FCSTD DOCUMENT  (FreeCAD 1.0R39319 (Git))
Label: Assy_Stack_Module_Flight_Cam
License: All rights reserved
LicenseURL: https://en.wikipedia.org/wiki/All_rights_reserved
objects: TechDraw::DrawViewBalloon×8, TechDraw::DrawViewDimension×6, TechDraw::DrawProjGroupItem×5, App::DocumentObjectGroup×3, App::Link×3, PartDesign::CoordinateSystem×2, TechDraw::DrawSVGTemplate×2, TechDraw::DrawPage×2, App::FeaturePython×1, Spreadsheet::Sheet×1, TechDraw::DrawViewSpreadsheet×1, TechDraw::DrawViewAnnotation×1, App::Part×1, TechDraw::DrawViewSection×1, TechDraw::DrawProjGroup×1
note: 6 computed .brp shape members not serialized (recipe doc carries the construction recipe); baked Part::Feature solids carry a one-line shape summary decoded from their .brp
EXTERNAL_REF file=Assy_Stack_Module.FCStd obj=LCS_Origin
EXTERNAL_REF file=Assy_Stack_Module.FCStd obj=Assembly
EXTERNAL_REF file=Assy_Flight_Cam.FCStd obj=LCS_Origin
EXTERNAL_REF file=Assy_Flight_Cam.FCStd obj=Assembly
EXTERNAL_REF file=../../Part/Print/Variants/IRFilter_Mount_1inchround.FCStd obj=LCS_1
EXTERNAL_REF file=../../Part/Print/Variants/IRFilter_Mount_1inchround.FCStd obj=Part

FEATURE [App::DocumentObjectGroup] Parts
FEATURE [PartDesign::CoordinateSystem] LCS_Origin
  AttacherType = Attacher::AttachEngine3D
  AttachmentSupport = -> [X_Axis]
  MapMode = 2
FEATURE [App::DocumentObjectGroup] Constraints
FEATURE [App::FeaturePython] Variables  # WARN: FeaturePython — macro-defined, semantics opaque (R4)
  Type = App::PropertyContainer
FEATURE [App::DocumentObjectGroup] Configurations
FEATURE [App::Link] Assy_Stack_Module
  AttachedBy = #LCS_Origin
  AttachedTo = Parent Assembly#LCS_Origin
  LinkedObject = -> <external Assy_Stack_Module.FCStd>#Assembly
  SolverId = Asm4EE
  expr: Placement = LCS_Origin.Placement * AttachmentOffset * Assy_Stack_Module#LCS_Origin.Placement ^ -1
FEATURE [App::Link] Assy_Flight_Cam
  AttachedBy = #LCS_Origin
  AttachedTo = Assy_Stack_Module#LCS_Origin
  AttachmentOffset = pos=(0,50,-41.75) rot=(0.57735,-0.57735,0.57735;2.0944rad)
  LinkPlacement = pos=(0,50,-41.75) rot=(0.57735,-0.57735,0.57735;2.0944rad)
  LinkedObject = -> <external Assy_Flight_Cam.FCStd>#Assembly
  Placement = pos=(0,50,-41.75) rot=(0.57735,-0.57735,0.57735;2.0944rad)
  SolverId = Asm4EE
  expr: Placement = Assy_Stack_Module.Placement * Assy_Stack_Module#LCS_Origin.Placement * AttachmentOffset * Assy_Flight_Cam#LCS_Origin.Placement ^ -1
FEATURE [PartDesign::CoordinateSystem] LCS_1
  AttacherType = Attacher::AttachEngine3D
FEATURE [Spreadsheet::Sheet] Spreadsheet  label="BOM"
  cells = A1=4; B1=2; C1='ISO 7380-2 M5x10 mm screw; D1='10–15 mm; ISO 4762 optional; A2=3; B2=4; C2='Spacer; D2='-; E2='PETG or PLA; A3=2; B3=3; C3='Stack_Module; D3='-; E3='PETG or PLA; A4=1; B4=1; C4='Eyeball Assembly; D4='-; A5='Position; B5='Quantity; C5='Part; D5='Dimensions; E5='Material
FEATURE [TechDraw::DrawSVGTemplate] Template
  EditableTexts = approval_person=GitHubPR; creator=Stefan; date_of_issue=20.03.2026; document_type=Assembly Drawing; general_tolerances=na; identification_number=na; language_code=EN; part_material=na; revision_index=AAA; scale=1 : 1; sheet_number=1 / 1; title=Assy_Stack_Module_Flight_Cam
  Height = 420
  Orientation = 1
  Template = <userpath>/Documents/PiTrac/3D Printed Parts/Enclosure Version 3/Assets/PiTrac_A2_Landscape_ISO5457_minimal.svg
  Width = 594
FEATURE [TechDraw::DrawViewSpreadsheet] Sheet
  CellEnd = E5
  CellStart = A1
  Font = osifont
  LineWidth = 0.35
  LockPosition = false
  Rotation = 0
  ScaleType = 2
  Source = -> Spreadsheet
  Symbol = <blob: 5666 chars omitted>
  TextSize = 12
  X = 491.96
  Y = 97.1596
FEATURE [TechDraw::DrawViewAnnotation] Annotation
  Font = osifont
  LineSpace = 100
  LockPosition = false
  MaxWidth = -1
  Rotation = 0
  ScaleType = 0
  Text = Not all parts are shown
  TextSize = 5
  TextStyle = 0
  X = 217.611
  Y = 30.4897
FEATURE [App::Link] IRFilter_Mount_1inchround
  AttachedBy = #LCS_1
  AttachedTo = Assy_Flight_Cam#LCS_Origin
  AttachmentOffset = pos=(0,34,0) rot=(0.57735,-0.57735,0.57735;2.0944rad)
  LinkPlacement = pos=(-34,50,-41.75) rot=(0.57735,-0.57735,0.57735;4.18879rad)
  LinkedObject = -> <external ../../Part/Print/Variants/IRFilter_Mount_1inchround.FCStd>#Part
  Placement = pos=(-34,50,-41.75) rot=(0.57735,-0.57735,0.57735;4.18879rad)
  SolverId = Asm4EE
  expr: Placement = Assy_Flight_Cam.Placement * Assy_Flight_Cam#LCS_Origin.Placement * AttachmentOffset * IRFilter_Mount_1inchround#LCS_1.Placement ^ -1
FEATURE [App::Part] Assembly  label="Assy_Stack_Module_Flight_Cam"
  AssemblyType = Part::Link
  Group = -> [LCS_Origin,Constraints,Variables,Configurations,Assy_Stack_Module,Assy_Flight_Cam,LCS_1,IRFilter_Mount_1inchround]
  Origin = -> Origin
  Type = Assembly
FEATURE [TechDraw::DrawProjGroupItem] View
  CoarseView = false
  Direction = (-0.57735,0.57735,-0.577351)
  Focus = 100
  HardHidden = false
  IsoCount = 0
  IsoHidden = false
  IsoVisible = false
  LockPosition = false
  Perspective = false
  Rotation = 0
  RotationVector = (1,0,0)
  Scale = 0.5
  ScaleType = 2
  ScrubCount = 1
  SeamHidden = false
  SeamVisible = false
  SmoothHidden = false
  SmoothVisible = true
  Source = -> [Assembly]
  Type = 0
  X = 343.081
  XDirection = (0.707107,0.707107,0)
  Y = 85.3438
FEATURE [TechDraw::DrawProjGroupItem] View001  label="Front"
  CoarseView = false
  Direction = (-1,0,0)
  Focus = 100
  HardHidden = false
  IsoCount = 0
  IsoHidden = false
  IsoVisible = false
  LockPosition = true
  Perspective = false
  Rotation = 0
  RotationVector = (1,0,0)
  ScaleType = 2
  ScrubCount = 1
  SeamHidden = false
  SeamVisible = false
  SmoothHidden = false
  SmoothVisible = true
  Source = -> [Assembly]
  Type = 0
  X = 0
  XDirection = (0,1,0)
  Y = 0
FEATURE [TechDraw::DrawProjGroupItem] ProjItem001  label="Left"
  CoarseView = false
  Direction = (-1e-16,-1,0)
  Focus = 100
  HardHidden = false
  IsoCount = 0
  IsoHidden = false
  IsoVisible = false
  LockPosition = false
  Perspective = false
  Rotation = 0
  RotationVector = (1,0,0)
  ScaleType = 0
  ScrubCount = 1
  SeamHidden = false
  SeamVisible = false
  SmoothHidden = false
  SmoothVisible = true
  Source = -> [Assembly]
  Type = 1
  X = 159
  XDirection = (-1,1e-16,0)
  Y = 0
FEATURE [TechDraw::DrawViewSection] SectionView  label="Section A - A"
  BaseView = -> View001
  CoarseView = false
  CutSurfaceDisplay = 2
  Direction = (0,1,0)
  FileGeomPattern = <path>\data\Mod/TechDraw/PAT/FCPAT.pat
  FileHatchPattern = <path>\data\Mod/TechDraw/Patterns/simple.svg
  Focus = 100
  FuseBeforeCut = false
  HardHidden = false
  HatchOffset = (0,0,0)
  HatchRotation = 0
  HatchScale = 1
  IsoCount = 0
  IsoHidden = false
  IsoVisible = false
  LockPosition = false
  NameGeomPattern = Diamond
  Perspective = false
  Rotation = 90
  ScaleType = 0
  ScrubCount = 1
  SeamHidden = false
  SeamVisible = false
  SectionDirection = 4
  SectionLineStretch = 1
  SectionNormal = (0,1,0)
  SectionOrigin = (19.99,50,-39.75)
  SectionSymbol = A
  SmoothHidden = false
  SmoothVisible = true
  Source = -> [Assembly]
  TrimAfterCut = false
  UsePreviousCut = false
  X = 376.166
  XDirection = (0,0,-1)
  Y = 208.818
FEATURE [TechDraw::DrawProjGroupItem] ProjItem  label="Top"
  CoarseView = false
  Direction = (0,0,-1)
  Focus = 100
  HardHidden = false
  IsoCount = 0
  IsoHidden = false
  IsoVisible = false
  LockPosition = false
  Perspective = false
  Rotation = 0
  RotationVector = (1,0,0)
  ScaleType = 0
  ScrubCount = 1
  SeamHidden = false
  SeamVisible = false
  SmoothHidden = false
  SmoothVisible = true
  Source = -> [Assembly]
  Type = 4
  X = 0
  XDirection = (0,1,0)
  Y = -131.75
FEATURE [TechDraw::DrawProjGroup] ProjGroup
  Anchor = -> View001
  AutoDistribute = true
  LockPosition = false
  ProjectionType = 0
  Rotation = 0
  ScaleType = 0
  Source = -> [Assembly]
  Views = -> [View001,ProjItem,ProjItem001]
  X = 135.715
  Y = 324.613
  spacingX = 15
  spacingY = 15
FEATURE [TechDraw::DrawViewBalloon] Balloon
  BubbleShape = 0
  EndType = 0
  EndTypeScale = 1
  KinkLength = 5
  LockPosition = false
  OriginX = -8.10485
  OriginY = -28.1923
  Rotation = 0
  ScaleType = 0
  ShapeScale = 1
  SourceView = -> ProjItem
  Text = 1
  TextWrapLen = -1
  X = -90
  Y = -44.8211
FEATURE [TechDraw::DrawViewBalloon] Balloon001
  BubbleShape = 0
  EndType = 0
  EndTypeScale = 1
  KinkLength = 5
  LockPosition = false
  OriginX = -59
  OriginY = 4.65153
  Rotation = 0
  ScaleType = 0
  ShapeScale = 1
  SourceView = -> ProjItem
  Text = 2
  TextWrapLen = -1
  X = -90
  Y = 7.51869
FEATURE [TechDraw::DrawViewBalloon] Balloon002
  BubbleShape = 0
  EndType = 0
  EndTypeScale = 1
  KinkLength = 5
  LockPosition = false
  OriginX = -63.6389
  OriginY = -53.0053
  Rotation = 0
  ScaleType = 0
  ShapeScale = 1
  SourceView = -> ProjItem
  Text = 3
  TextWrapLen = -1
  X = -90
  Y = -71.4065
FEATURE [TechDraw::DrawViewBalloon] Balloon003
  BubbleShape = 0
  EndType = 0
  EndTypeScale = 1
  KinkLength = 5
  LockPosition = false
  OriginX = 63.25
  OriginY = -53.5
  Rotation = 0
  ScaleType = 0
  ShapeScale = 1
  SourceView = -> ProjItem
  Text = 3
  TextWrapLen = -1
  X = 90
  Y = -71.3104
FEATURE [TechDraw::DrawViewBalloon] Balloon005
  BubbleShape = 0
  EndType = 0
  EndTypeScale = 1
  KinkLength = 5
  LockPosition = false
  OriginX = 60.25
  OriginY = 62.5
  Rotation = 0
  ScaleType = 0
  ShapeScale = 1
  SourceView = -> ProjItem
  Text = 3
  TextWrapLen = -1
  X = 90
  Y = 35.237
FEATURE [TechDraw::DrawViewBalloon] Balloon006
  BubbleShape = 0
  EndType = 0
  EndTypeScale = 1
  KinkLength = 5
  LockPosition = false
  OriginX = -59.5034
  OriginY = 64.5614
  Rotation = 0
  ScaleType = 0
  ShapeScale = 1
  SourceView = -> ProjItem
  Text = 3
  TextWrapLen = -1
  X = -90
  Y = 62.1115
FEATURE [TechDraw::DrawViewBalloon] Balloon007
  BubbleShape = 0
  EndType = 0
  EndTypeScale = 1
  KinkLength = 5
  LockPosition = false
  OriginX = -51.8231
  OriginY = -46.9426
  Rotation = 0
  ScaleType = 0
  ShapeScale = 1
  SourceView = -> View001
  Text = 4
  TextWrapLen = -1
  X = -90
  Y = -51.1449
FEATURE [TechDraw::DrawViewBalloon] Balloon008
  BubbleShape = 0
  EndType = 0
  EndTypeScale = 1
  KinkLength = 5
  LockPosition = false
  OriginX = 52.1555
  OriginY = -45.761
  Rotation = 0
  ScaleType = 0
  ShapeScale = 1
  SourceView = -> View001
  Text = 4
  TextWrapLen = -1
  X = 90
  Y = -74.0359
FEATURE [TechDraw::DrawViewDimension] Dimension001
  AngleOverride = false
  Arbitrary = false
  ArbitraryTolerances = false
  BoxCorners = (2) [(-74,-70,-1e-07),(74,70,1e-07)]
  EqualTolerance = true
  ExtensionAngle = 0
  FormatSpec = %.2w
  FormatSpecOverTolerance = %+.2w
  FormatSpecUnderTolerance = %+.2w
  Inverted = false
  LineAngle = 0
  LockPosition = false
  MeasureType = 1
  OverTolerance = 0
  References2D = -> [ProjItem]
  Rotation = 0
  ScaleType = 0
  TheoreticalExact = false
  Type = 0
  UnderTolerance = 0
  X = -3.00169
  Y = -115.966
FEATURE [TechDraw::DrawViewDimension] Dimension002
  AngleOverride = false
  Arbitrary = false
  ArbitraryTolerances = false
  BoxCorners = (2) [(-70,-46,-1e-07),(70,46,1e-07)]
  EqualTolerance = true
  ExtensionAngle = 0
  FormatSpec = %.2w
  FormatSpecOverTolerance = %+.2w
  FormatSpecUnderTolerance = %+.2w
  Inverted = false
  LineAngle = 0
  LockPosition = false
  MeasureType = 1
  OverTolerance = 0
  References2D = -> [ProjItem001]
  Rotation = 0
  ScaleType = 0
  TheoreticalExact = false
  Type = 0
  UnderTolerance = 0
  X = 110.964
  Y = 0.25
FEATURE [TechDraw::DrawViewDimension] Dimension003
  AngleOverride = false
  Arbitrary = false
  ArbitraryTolerances = false
  BoxCorners = (2) [(-70,-46,-1e-07),(70,46,1e-07)]
  EqualTolerance = true
  ExtensionAngle = 0
  FormatSpec = %.2w
  FormatSpecOverTolerance = %+.2w
  FormatSpecUnderTolerance = %+.2w
  Inverted = false
  LineAngle = 0
  LockPosition = false
  MeasureType = 1
  OverTolerance = 0
  References2D = -> [ProjItem001]
  Rotation = 0
  ScaleType = 0
  TheoreticalExact = false
  Type = 0
  UnderTolerance = 0
  X = 149.356
  Y = 1.25
FEATURE [TechDraw::DrawViewDimension] Dimension004
  AngleOverride = false
  Arbitrary = false
  ArbitraryTolerances = false
  BoxCorners = (2) [(-74,-70,-1e-07),(74,70,1e-07)]
  EqualTolerance = true
  ExtensionAngle = 0
  FormatSpec = %.2w
  FormatSpecOverTolerance = %+.2w
  FormatSpecUnderTolerance = %+.2w
  Inverted = false
  LineAngle = 0
  LockPosition = false
  MeasureType = 1
  OverTolerance = 0
  References2D = -> [ProjItem]
  Rotation = 0
  ScaleType = 0
  TheoreticalExact = false
  Type = 0
  UnderTolerance = 0
  X = 126.237
  Y = 5
FEATURE [TechDraw::DrawSVGTemplate] Template001
  Height = 210
  Orientation = 1
  Template = C:/Program Files/FreeCAD 1.0/data/Mod/TechDraw/Templates/Default_Template_A4_Landscape.svg
  Width = 297
FEATURE [TechDraw::DrawProjGroupItem] View002
  CoarseView = false
  Direction = (-0.57735,0.57735,-0.577351)
  Focus = 100
  HardHidden = false
  IsoCount = 0
  IsoHidden = false
  IsoVisible = false
  LockPosition = false
  Perspective = false
  Rotation = 0
  RotationVector = (1,0,0)
  ScaleType = 0
  ScrubCount = 1
  SeamHidden = false
  SeamVisible = false
  SmoothHidden = false
  SmoothVisible = true
  Source = -> [Assembly]
  Type = 0
  X = 148.5
  XDirection = (0.707107,0.707107,0)
  Y = 105
FEATURE [TechDraw::DrawPage] Page001
  KeepUpdated = true
  NextBalloonIndex = 1
  ProjectionType = 0
  Template = -> Template001
  Views = -> [View002]
FEATURE [TechDraw::DrawViewDimension] Dimension
  AngleOverride = false
  Arbitrary = false
  ArbitraryTolerances = false
  BoxCorners = (2) [(-74,-70,-1e-07),(74,70,1e-07)]
  EqualTolerance = true
  ExtensionAngle = 0
  FormatSpec = %.1w
  FormatSpecOverTolerance = %+.2w
  FormatSpecUnderTolerance = %+.2w
  Inverted = false
  LineAngle = 0
  LockPosition = false
  MeasureType = 1
  OverTolerance = 0
  References2D = -> [ProjItem]
  Rotation = 0
  ScaleType = 0
  TheoreticalExact = false
  Type = 2
  UnderTolerance = 0
  X = 103.142
  Y = -44.9928
FEATURE [TechDraw::DrawViewDimension] Dimension005
  AngleOverride = false
  Arbitrary = false
  ArbitraryTolerances = false
  BoxCorners = (2) [(-70,-46.125,-1e-07),(70,46.125,1e-07)]
  EqualTolerance = true
  ExtensionAngle = 0
  FormatSpec = %.1w
  FormatSpecOverTolerance = %+.2w
  FormatSpecUnderTolerance = %+.2w
  Inverted = false
  LineAngle = 0
  LockPosition = false
  MeasureType = 1
  OverTolerance = 0
  References2D = -> [SectionView]
  Rotation = 0
  ScaleType = 0
  TheoreticalExact = false
  Type = 0
  UnderTolerance = 0
  X = -39.9928
  Y = -51.5552
FEATURE [TechDraw::DrawPage] Page
  KeepUpdated = true
  NextBalloonIndex = 11
  ProjectionType = 0
  Template = -> Template
  Views = -> [Sheet,View,ProjGroup,SectionView,Balloon,Balloon001,Balloon002,Balloon003,Balloon005,Balloon006,Balloon007,Balloon008,Dimension001,Dimension002,Dimension003,Dimension004,Annotation,Dimension,Dimension005]
note: 2 file-system paths scrubbed to <path> (originals preserved in the JSON sidecar)

RESOLVED EXTERNAL PARTS (link-assembly join: the EXTERNAL_REF files above that resolve inside this repo's crawl, each included once):
---- part ../../Part/Print/Variants/IRFilter_Mount_1inchround.FCStd = doc fcstd_7a37d6c983e9 ----
FCSTD DOCUMENT  (FreeCAD 1.0R39319 (Git))
Label: IRFilter_Mount_1inchround
License: All rights reserved
LicenseURL: https://en.wikipedia.org/wiki/All_rights_reserved
objects: Sketcher::SketchObject×3, PartDesign::Pad×1, PartDesign::Groove×1, PartDesign::Pocket×1, PartDesign::PolarPattern×1, PartDesign::Body×1, PartDesign::CoordinateSystem×1, App::Part×1
note: 19 computed .brp shape members not serialized (recipe doc carries the construction recipe); baked Part::Feature solids carry a one-line shape summary decoded from their .brp

FEATURE [Sketcher::SketchObject] Sketch
  ArcFitTolerance = 1e-06
  AttachmentSupport = -> [XY_Plane001]
  FullyConstrained = true
  MakeInternals = false
  MapMode = 5
  sketch-geometry (1):
    g0: Circle CenterX=0 CenterY=0 CenterZ=0 NormalX=0 NormalY=0 NormalZ=1 AngleXU=0 Radius=17
  constraints (2):
    c: Coincident(g0,g-1)
    c: Diameter(g0) = 34
FEATURE [PartDesign::Pad] Pad
  Direction = (0,0,1)
  Length = 10
  Length2 = 10
  Profile = -> Sketch
  ReferenceAxis = -> Sketch [N_Axis]
  Refine = true
  Suppressed = false
  Type = 0
FEATURE [Sketcher::SketchObject] Sketch001
  ArcFitTolerance = 1e-06
  AttachmentSupport = -> [YZ_Plane001]
  ExternalGeometry = -> [Pad]
  FullyConstrained = true
  MakeInternals = false
  MapMode = 5
  Placement = pos=(0,0,0) rot=(0.57735,0.57735,0.57735;2.0944rad)
  sketch-geometry (13):
    g0: LineSegment StartX=0 StartY=0 StartZ=0 EndX=0 EndY=10 EndZ=0
    g1: LineSegment StartX=0 StartY=10 StartZ=0 EndX=16 EndY=10 EndZ=0
    g2: LineSegment StartX=16 StartY=10 StartZ=0 EndX=15 EndY=8.26795 EndZ=0
    g3: LineSegment StartX=15 StartY=8.26795 StartZ=0 EndX=16 EndY=1.5 EndZ=0
    g4: LineSegment StartX=16 StartY=1.5 StartZ=0 EndX=13.7 EndY=1.5 EndZ=0
    g5: LineSegment StartX=13.7 StartY=1.5 StartZ=0 EndX=13.7 EndY=2.7 EndZ=0
    g6: LineSegment StartX=13.7 StartY=2.7 StartZ=0 EndX=13.1 EndY=2.7 EndZ=0
    g7: LineSegment StartX=13.1 StartY=2.7 StartZ=0 EndX=13.1 EndY=1.5 EndZ=0
    g8: LineSegment StartX=13.1 StartY=1.5 StartZ=0 EndX=12.6 EndY=1.5 EndZ=0
    g9: LineSegment StartX=12.6 StartY=1.5 StartZ=0 EndX=12.6 EndY=0 EndZ=0
    g10: LineSegment StartX=12.6 StartY=0 StartZ=0 EndX=0 EndY=0 EndZ=0
    g11: LineSegment [constr] StartX=13.1 StartY=1.5 StartZ=0 EndX=13.7 EndY=1.5 EndZ=0
    g12: LineSegment [constr] StartX=16 StartY=1.5 StartZ=0 EndX=16 EndY=10 EndZ=0
  constraints (36):
    c: Coincident(g-1,g0)
    c: PointOnObject(g0,g-2)
    c: Coincident(g0,g1)
    c: Horizontal(g1)
    c: Coincident(g1,g2)
    c: Coincident(g2,g3)
    c: Coincident(g3,g4)
    c: Horizontal(g4)
    c: Coincident(g4,g5)
    c: Vertical(g5)
    c: Coincident(g5,g6)
    c: Horizontal(g6)
    c: Coincident(g6,g7)
    c: Vertical(g7)
    c: Coincident(g7,g8)
    c: Horizontal(g8)
    c: Coincident(g8,g9)
    c: PointOnObject(g9,g-1)
    c: Coincident(g9,g10)
    c: Coincident(g10,g0)
    c: PointOnObject(g0,g-3)
    c: Angle(g1,g2) = 1.0472
    c: Vertical(g9)
    c: Distance(g7,g9) = 0.5
    c: Distance(g5,g7) = 0.6
    c: Distance(g6,g4) = 1.2
    c: Distance(g8,g10) = 1.5
    c: DistanceX(g-1,g2) = 15
    c: DistanceX(g-1,g1) = 16
    c: Coincident(g11,g7)
    c: Coincident(g11,g4)
    c: Coincident(g12,g3)
    c: Coincident(g12,g1)
    c: Vertical(g12)
    c: Horizontal(g11)
    c: DistanceX(g-1,g6) = 13.1
FEATURE [PartDesign::Groove] Groove
  Angle = 360
  Angle2 = 60
  Axis = (0,0,1)
  Base = (0,0,0)
  BaseFeature = -> Pad
  Profile = -> Sketch001
  ReferenceAxis = -> Sketch001 [V_Axis]
  Refine = true
  Suppressed = false
  Type = 0
FEATURE [Sketcher::SketchObject] Sketch002
  ArcFitTolerance = 1e-06
  AttachmentSupport = -> [XZ_Plane001]
  ExternalGeometry = -> [Groove]
  FullyConstrained = true
  MakeInternals = false
  MapMode = 5
  Placement = pos=(0,0,0) rot=(1,0,0;1.5708rad)
  sketch-geometry (4):
    g0: LineSegment StartX=-1.25 StartY=10 StartZ=0 EndX=1.25 EndY=10 EndZ=0
    g1: LineSegment StartX=1.25 StartY=10 StartZ=0 EndX=1.25 EndY=5 EndZ=0
    g2: ArcOfCircle CenterX=-1e-16 CenterY=5 CenterZ=0 NormalX=0 NormalY=0 NormalZ=1 AngleXU=0 Radius=1.25 StartAngle=3.14159 EndAngle=6.28319
    g3: LineSegment StartX=-1.25 StartY=5 StartZ=0 EndX=-1.25 EndY=10 EndZ=0
  constraints (10):
    c: Coincident(g0,g1)
    c: Vertical(g1)
    c: Tangent(g1,g2) = 1.5708
    c: Tangent(g2,g3) = 1.5708
    c: Coincident(g3,g0)
    c: Vertical(g3)
    c: Distance(g1,g3) = 2.5
    c: PointOnObject(g0,g-3)
    c: Symmetric(g0,g0,g-2)
    c: Distance(g2,g0) = 5
FEATURE [PartDesign::Pocket] Pocket
  BaseFeature = -> Groove
  Direction = (0,1,-2e-16)
  Length = 5
  Length2 = 5
  Midplane = true
  Profile = -> Sketch002
  ReferenceAxis = -> Sketch002 [N_Axis]
  Refine = true
  Suppressed = false
  Type = 1
FEATURE [PartDesign::PolarPattern] PolarPattern
  Angle = 90
  Axis = -> Z_Axis001
  BaseFeature = -> Pocket
  Mode = 0
  Occurrences = 2
  Offset = 120
  Originals = -> [Pocket]
  Refine = true
  Suppressed = false
  TransformMode = 0
FEATURE [PartDesign::Body] Body
  AllowCompound = false
  Group = -> [Sketch,Pad,Sketch001,Groove,Sketch002,Pocket,PolarPattern]
  Origin = -> Origin001
  Tip = -> PolarPattern
FEATURE [PartDesign::CoordinateSystem] LCS_1
  AttacherType = Attacher::AttachEngine3D
FEATURE [App::Part] Part  label="IRFilter_Mount_1inchround"
  Group = -> [Body,LCS_1]
  Origin = -> Origin
---- part Assy_Flight_Cam.FCStd = doc fcstd_9f404098250c ----
FCSTD DOCUMENT  (FreeCAD 1.0R39319 (Git))
Label: Assy_Flight_Cam
License: All rights reserved
LicenseURL: https://en.wikipedia.org/wiki/All_rights_reserved
objects: TechDraw::DrawViewBalloon×11, TechDraw::DrawProjGroupItem×7, TechDraw::DrawViewDimension×4, App::DocumentObjectGroup×3, App::Link×3, TechDraw::DrawSVGTemplate×2, TechDraw::DrawPage×2, PartDesign::CoordinateSystem×1, App::FeaturePython×1, App::Part×1, TechDraw::DrawViewSection×1, TechDraw::DrawProjGroup×1, Spreadsheet::Sheet×1, TechDraw::DrawViewSpreadsheet×1, TechDraw::DrawViewAnnotation×1
note: 9 computed .brp shape members not serialized (recipe doc carries the construction recipe); baked Part::Feature solids carry a one-line shape summary decoded from their .brp
EXTERNAL_REF file=Assy_Camera_Eyeball.FCStd obj=LCS_Origin
EXTERNAL_REF file=Assy_Camera_Eyeball.FCStd obj=Assembly
EXTERNAL_REF file=Assy_EyeScreen.FCStd obj=LCS_Origin
EXTERNAL_REF file=Assy_EyeScreen.FCStd obj=Assembly
EXTERNAL_REF file=Assy_EyeScreen_Clamp.FCStd obj=LCS_Origin
EXTERNAL_REF file=Assy_EyeScreen_Clamp.FCStd obj=Assembly

FEATURE [App::DocumentObjectGroup] Parts
FEATURE [PartDesign::CoordinateSystem] LCS_Origin
  AttacherType = Attacher::AttachEngine3D
  AttachmentSupport = -> [X_Axis]
  MapMode = 2
FEATURE [App::DocumentObjectGroup] Constraints
FEATURE [App::FeaturePython] Variables  # WARN: FeaturePython — macro-defined, semantics opaque (R4)
  Type = App::PropertyContainer
FEATURE [App::DocumentObjectGroup] Configurations
FEATURE [App::Link] Assy_Camera_Eyeball
  AttachedBy = #LCS_Origin
  AttachedTo = Parent Assembly#LCS_Origin
  LinkedObject = -> <external Assy_Camera_Eyeball.FCStd>#Assembly
  SolverId = Asm4EE
  expr: Placement = LCS_Origin.Placement * AttachmentOffset * Assy_Camera_Eyeball#LCS_Origin.Placement ^ -1
FEATURE [App::Link] Assy_EyeScreen
  AttachedBy = #LCS_Origin
  AttachedTo = Parent Assembly#LCS_Origin
  AttachmentOffset = pos=(0,0,0) rot=(0.57735,0.57735,-0.57735;4.18879rad)
  LinkPlacement = pos=(0,0,0) rot=(0.57735,0.57735,-0.57735;4.18879rad)
  LinkedObject = -> <external Assy_EyeScreen.FCStd>#Assembly
  Placement = pos=(0,0,0) rot=(0.57735,0.57735,-0.57735;4.18879rad)
  SolverId = Asm4EE
  expr: Placement = LCS_Origin.Placement * AttachmentOffset * Assy_EyeScreen#LCS_Origin.Placement ^ -1
FEATURE [App::Link] Assy_EyeScreen_Clamp
  AttachedBy = #LCS_Origin
  AttachedTo = Parent Assembly#LCS_Origin
  AttachmentOffset = pos=(0,0,0) rot=(-0.57735,-0.57735,0.57735;4.18879rad)
  LinkPlacement = pos=(0,0,0) rot=(-0.57735,-0.57735,0.57735;4.18879rad)
  LinkedObject = -> <external Assy_EyeScreen_Clamp.FCStd>#Assembly
  Placement = pos=(0,0,0) rot=(-0.57735,-0.57735,0.57735;4.18879rad)
  SolverId = Asm4EE
  expr: Placement = LCS_Origin.Placement * AttachmentOffset * Assy_EyeScreen_Clamp#LCS_Origin.Placement ^ -1
FEATURE [App::Part] Assembly  label="Assy_Flight_Cam"
  AssemblyType = Part::Link
  Group = -> [LCS_Origin,Constraints,Variables,Configurations,Assy_Camera_Eyeball,Assy_EyeScreen,Assy_EyeScreen_Clamp]
  Origin = -> Origin
  Type = Assembly
FEATURE [TechDraw::DrawSVGTemplate] Template
  EditableTexts = approval_person=GitHubPR; creator=Stefan; date_of_issue=20.03.2026; document_type=Assembly Drawing; general_tolerances=na; identification_number=na; language_code=EN; part_material=na; revision_index=AAA; scale=1 : 1; sheet_number=1 / 1; title=Assy_Flight_Cam
  Height = 420
  Orientation = 1
  Template = <userpath>/Documents/PiTrac/3D Printed Parts/Enclosure Version 3/Assets/PiTrac_A2_Landscape_ISO5457_minimal.svg
  Width = 594
FEATURE [TechDraw::DrawProjGroupItem] View
  CoarseView = false
  Direction = (-0.57735,0.57735,-0.57735)
  Focus = 100
  HardHidden = false
  IsoCount = 0
  IsoHidden = false
  IsoVisible = false
  LockPosition = false
  Perspective = false
  Rotation = 0
  RotationVector = (1,0,0)
  ScaleType = 0
  ScrubCount = 1
  SeamHidden = false
  SeamVisible = false
  SmoothHidden = false
  SmoothVisible = true
  Source = -> [Assembly]
  Type = 0
  X = 339.537
  XDirection = (0,-0.707106,-0.707106)
  Y = 100.114
FEATURE [TechDraw::DrawProjGroupItem] View001  label="Front"
  CoarseView = false
  Direction = (0,1,0)
  Focus = 100
  HardHidden = false
  IsoCount = 0
  IsoHidden = false
  IsoVisible = false
  LockPosition = true
  Perspective = false
  Rotation = 0
  RotationVector = (1,0,0)
  ScaleType = 2
  ScrubCount = 1
  SeamHidden = false
  SeamVisible = false
  SmoothHidden = false
  SmoothVisible = true
  Source = -> [Assembly]
  Type = 0
  X = 0
  XDirection = (0,0,-1)
  Y = 0
FEATURE [TechDraw::DrawProjGroupItem] ProjItem  label="Top"
  CoarseView = false
  Direction = (-1,0,0)
  Focus = 100
  HardHidden = false
  IsoCount = 0
  IsoHidden = false
  IsoVisible = false
  LockPosition = false
  Perspective = false
  Rotation = 0
  RotationVector = (1,0,0)
  ScaleType = 0
  ScrubCount = 1
  SeamHidden = false
  SeamVisible = false
  SmoothHidden = false
  SmoothVisible = true
  Source = -> [Assembly]
  Type = 4
  X = 0
  XDirection = (0,0,-1)
  Y = -87.3862
FEATURE [TechDraw::DrawProjGroupItem] ProjItem001  label="Left"
  CoarseView = false
  Direction = (0,1e-16,1)
  Focus = 100
  HardHidden = false
  IsoCount = 0
  IsoHidden = false
  IsoVisible = false
  LockPosition = false
  Perspective = false
  Rotation = 0
  RotationVector = (1,0,0)
  ScaleType = 0
  ScrubCount = 1
  SeamHidden = false
  SeamVisible = false
  SmoothHidden = false
  SmoothVisible = true
  Source = -> [Assembly]
  Type = 1
  X = 98.664
  XDirection = (0,1,-1e-16)
  Y = 0
FEATURE [TechDraw::DrawProjGroupItem] ProjItem002  label="Rear"
  CoarseView = false
  Direction = (0,-1,0)
  Focus = 100
  HardHidden = false
  IsoCount = 0
  IsoHidden = false
  IsoVisible = false
  LockPosition = false
  Perspective = false
  Rotation = 0
  RotationVector = (1,0,0)
  ScaleType = 0
  ScrubCount = 1
  SeamHidden = false
  SeamVisible = false
  SmoothHidden = false
  SmoothVisible = true
  Source = -> [Assembly]
  Type = 3
  X = 197.325
  XDirection = (0,0,1)
  Y = 0
FEATURE [TechDraw::DrawViewSection] SectionView  label="Section A - A"
  BaseView = -> View001
  CoarseView = false
  CutSurfaceDisplay = 2
  Direction = (-1,0,-1e-16)
  FileGeomPattern = <path>\data\Mod/TechDraw/PAT/FCPAT.pat
  FileHatchPattern = <path>\data\Mod/TechDraw/Patterns/simple.svg
  Focus = 100
  FuseBeforeCut = false
  HardHidden = false
  HatchOffset = (0,0,0)
  HatchRotation = 0
  HatchScale = 1
  IsoCount = 0
  IsoHidden = false
  IsoVisible = false
  LockPosition = false
  NameGeomPattern = Diamond
  Perspective = false
  Rotation = 0
  ScaleType = 0
  ScrubCount = 1
  SeamHidden = false
  SeamVisible = false
  SectionDirection = 4
  SectionLineStretch = 1
  SectionNormal = (-1,0,-1e-16)
  SectionOrigin = (0,3.24,0)
  SectionSymbol = A
  SmoothHidden = false
  SmoothVisible = true
  Source = -> [Assembly]
  TrimAfterCut = false
  UsePreviousCut = false
  X = 132.761
  XDirection = (1e-16,0,-1)
  Y = 93.6148
FEATURE [TechDraw::DrawProjGroupItem] ProjItem003  label="Bottom"
  CoarseView = false
  Direction = (1,0,0)
  Focus = 100
  HardHidden = false
  IsoCount = 0
  IsoHidden = false
  IsoVisible = false
  LockPosition = false
  Perspective = false
  Rotation = 0
  RotationVector = (1,0,0)
  ScaleType = 0
  ScrubCount = 1
  SeamHidden = false
  SeamVisible = false
  SmoothHidden = false
  SmoothVisible = true
  Source = -> [Assembly]
  Type = 5
  X = 0
  XDirection = (0,0,-1)
  Y = 87.3862
FEATURE [TechDraw::DrawProjGroup] ProjGroup
  Anchor = -> View001
  AutoDistribute = true
  LockPosition = false
  ProjectionType = 0
  Rotation = 0
  ScaleType = 0
  Source = -> [Assembly]
  Views = -> [View001,ProjItem,ProjItem001,ProjItem002,ProjItem003]
  X = 132.761
  Y = 274.987
  spacingX = 15
  spacingY = 15
FEATURE [Spreadsheet::Sheet] Spreadsheet  label="BOM"
  cells = A1=5; B1=4; C1='ISO 7380-2 M5x20 mm screw; D1='20–25 mm; ISO 4762 optional; A2=4; B2=4; C2='ISO 4032 M5 nut; A3=3; B3=1; C3='EyeScreen_Clamp; D3='8-12 mm ; E3='PETG or PLA; A4=2; B4=1; C4='EyeScreen; D4='-; E4='PETG or PLA; A5=1; B5=1; C5='Camera or LED Assembly; D5='-; A6='Position; B6='Quantity; C6='Part; D6='Dimensions; E6='Material
FEATURE [TechDraw::DrawViewSpreadsheet] Sheet
  CellEnd = E6
  CellStart = A1
  Font = osifont
  LineWidth = 0.35
  LockPosition = false
  Rotation = 0
  ScaleType = 2
  Source = -> Spreadsheet
  Symbol = <blob: 6751 chars omitted>
  TextSize = 12
  X = 491.96
  Y = 112.52
FEATURE [TechDraw::DrawViewBalloon] Balloon
  BubbleShape = 0
  EndType = 0
  EndTypeScale = 1
  KinkLength = 5
  LockPosition = false
  OriginX = -14.5739
  OriginY = -27.7259
  Rotation = 0
  ScaleType = 0
  ShapeScale = 1
  SourceView = -> ProjItem
  Text = 1
  TextWrapLen = -1
  X = -85
  Y = -42.6008
FEATURE [TechDraw::DrawViewBalloon] Balloon001
  BubbleShape = 0
  EndType = 0
  EndTypeScale = 1
  KinkLength = 5
  LockPosition = false
  OriginX = -13.1208
  OriginY = -5.9291
  Rotation = 0
  ScaleType = 0
  ShapeScale = 1
  SourceView = -> ProjItem
  Text = 2
  TextWrapLen = -1
  X = -85
  Y = -17.8977
FEATURE [TechDraw::DrawViewBalloon] Balloon002
  BubbleShape = 0
  EndType = 0
  EndTypeScale = 1
  KinkLength = 5
  LockPosition = false
  OriginX = -12.152
  OriginY = 11.024
  Rotation = 0
  ScaleType = 0
  ShapeScale = 1
  SourceView = -> ProjItem
  Text = 3
  TextWrapLen = -1
  X = -85
  Y = 15.524
FEATURE [TechDraw::DrawViewBalloon] Balloon003
  BubbleShape = 0
  EndType = 0
  EndTypeScale = 1
  KinkLength = 5
  LockPosition = false
  OriginX = 41.129
  OriginY = -28.4405
  Rotation = 0
  ScaleType = 0
  ShapeScale = 1
  SourceView = -> View001
  Text = 5
  TextWrapLen = -1
  X = -85
  Y = -45.7373
FEATURE [TechDraw::DrawViewBalloon] Balloon004
  BubbleShape = 0
  EndType = 0
  EndTypeScale = 1
  KinkLength = 5
  LockPosition = false
  OriginX = -45.0894
  OriginY = -26.0187
  Rotation = 0
  ScaleType = 0
  ShapeScale = 1
  SourceView = -> View001
  Text = 5
  TextWrapLen = -1
  X = -85
  Y = -23.4561
FEATURE [TechDraw::DrawViewBalloon] Balloon005
  BubbleShape = 0
  EndType = 0
  EndTypeScale = 1
  KinkLength = 5
  LockPosition = false
  OriginX = -44.6051
  OriginY = 24.3562
  Rotation = 0
  ScaleType = 0
  ShapeScale = 1
  SourceView = -> View001
  Text = 5
  TextWrapLen = -1
  X = -85
  Y = 10.45
FEATURE [TechDraw::DrawViewBalloon] Balloon006
  BubbleShape = 0
  EndType = 0
  EndTypeScale = 1
  KinkLength = 5
  LockPosition = false
  OriginX = 41.6134
  OriginY = 25.3249
  Rotation = 0
  ScaleType = 0
  ShapeScale = 1
  SourceView = -> Balloon005
  Text = 5
  TextWrapLen = -1
  X = -85
  Y = 38.0593
FEATURE [TechDraw::DrawViewBalloon] Balloon007
  BubbleShape = 0
  EndType = 0
  EndTypeScale = 1
  KinkLength = 5
  LockPosition = false
  OriginX = -44.4406
  OriginY = 27.2624
  Rotation = 0
  ScaleType = 0
  ShapeScale = 1
  SourceView = -> ProjItem002
  Text = 4
  TextWrapLen = -1
  X = -35
  Y = 60
FEATURE [TechDraw::DrawViewBalloon] Balloon008
  BubbleShape = 0
  EndType = 0
  EndTypeScale = 1
  KinkLength = 5
  LockPosition = false
  OriginX = 41.7778
  OriginY = 27.2624
  Rotation = 0
  ScaleType = 0
  ShapeScale = 1
  SourceView = -> Balloon007
  Text = 4
  TextWrapLen = -1
  X = 35
  Y = 60
FEATURE [TechDraw::DrawViewBalloon] Balloon009
  BubbleShape = 0
  EndType = 0
  EndTypeScale = 1
  KinkLength = 5
  LockPosition = false
  OriginX = -41.5344
  OriginY = -26.9874
  Rotation = 0
  ScaleType = 0
  ShapeScale = 1
  SourceView = -> Balloon008
  Text = 4
  TextWrapLen = -1
  X = -35
  Y = -60
FEATURE [TechDraw::DrawViewBalloon] Balloon010
  BubbleShape = 0
  EndType = 0
  EndTypeScale = 1
  KinkLength = 5
  LockPosition = false
  OriginX = 44.6841
  OriginY = -27.4718
  Rotation = 0
  ScaleType = 0
  ShapeScale = 1
  SourceView = -> Balloon009
  Text = 4
  TextWrapLen = -1
  X = 35
  Y = -60
FEATURE [TechDraw::DrawViewDimension] Dimension
  AngleOverride = false
  Arbitrary = false
  ArbitraryTolerances = false
  BoxCorners = (2) [(-55,-41.75,-1e-07),(55,41.75,1e-07)]
  EqualTolerance = true
  ExtensionAngle = 0
  FormatSpec = %.2w
  FormatSpecOverTolerance = %+.2w
  FormatSpecUnderTolerance = %+.2w
  Inverted = false
  LineAngle = 0
  LockPosition = false
  MeasureType = 1
  OverTolerance = 0
  References2D = -> [ProjItem002]
  Rotation = 0
  ScaleType = 0
  TheoreticalExact = false
  Type = 0
  UnderTolerance = 0
  X = 0
  Y = 75.2623
FEATURE [TechDraw::DrawViewDimension] Dimension002
  AngleOverride = false
  Arbitrary = false
  ArbitraryTolerances = false
  BoxCorners = (2) [(-55,-27.7612,-1e-07),(55,27.7612,1e-07)]
  EqualTolerance = true
  ExtensionAngle = 0
  FormatSpec = %.2w
  FormatSpecOverTolerance = %+.2w
  FormatSpecUnderTolerance = %+.2w
  Inverted = false
  LineAngle = 0
  LockPosition = false
  MeasureType = 1
  OverTolerance = 0
  References2D = -> [ProjItem]
  Rotation = 0
  ScaleType = 0
  TheoreticalExact = false
  Type = 0
  UnderTolerance = 0
  X = 80.4534
  Y = -0.761239
FEATURE [TechDraw::DrawViewAnnotation] Annotation
  Font = osifont
  LineSpace = 100
  LockPosition = false
  MaxWidth = -1
  Rotation = 0
  ScaleType = 0
  Text = Not all parts are shown
  TextSize = 5
  TextStyle = 0
  X = 248.802
  Y = 28.3711
FEATURE [TechDraw::DrawViewDimension] Dimension004
  AngleOverride = false
  Arbitrary = false
  ArbitraryTolerances = false
  BoxCorners = (2) [(-55,-41.75,-1e-07),(55,41.75,1e-07)]
  EqualTolerance = true
  ExtensionAngle = 0
  FormatSpec = %.2w
  FormatSpecOverTolerance = %+.2w
  FormatSpecUnderTolerance = %+.2w
  Inverted = false
  LineAngle = 0
  LockPosition = false
  MeasureType = 1
  OverTolerance = 0
  References2D = -> [ProjItem002]
  Rotation = 0
  ScaleType = 0
  TheoreticalExact = false
  Type = 0
  UnderTolerance = 0
  X = 122.276
  Y = 0
FEATURE [TechDraw::DrawViewDimension] Dimension005
  AngleOverride = false
  Arbitrary = false
  ArbitraryTolerances = false
  BoxCorners = (2) [(-55,-27.7612,-1e-07),(55,27.7612,1e-07)]
  EqualTolerance = true
  ExtensionAngle = 0
  FormatSpec = %.2w
  FormatSpecOverTolerance = %+.2w
  FormatSpecUnderTolerance = %+.2w
  Inverted = false
  LineAngle = 0
  LockPosition = false
  MeasureType = 1
  OverTolerance = 0
  References2D = -> [SectionView]
  Rotation = 0
  ScaleType = 0
  TheoreticalExact = false
  Type = 0
  UnderTolerance = 0
  X = 83.0603
  Y = 10.2655
FEATURE [TechDraw::DrawPage] Page
  KeepUpdated = true
  NextBalloonIndex = 12
  ProjectionType = 0
  Template = -> Template
  Views = -> [View,ProjGroup,SectionView,Sheet,Balloon,Balloon001,Balloon002,Balloon003,Balloon004,Balloon005,Balloon006,Balloon007,Balloon008,Balloon009,Balloon010,Dimension,Dimension002,Annotation,Dimension004,Dimension005]
FEATURE [TechDraw::DrawSVGTemplate] Template001
  Height = 210
  Orientation = 1
  Template = C:/Program Files/FreeCAD 1.0/data/Mod/TechDraw/Templates/Default_Template_A4_Landscape.svg
  Width = 297
FEATURE [TechDraw::DrawProjGroupItem] View002
  CoarseView = false
  Direction = (-0.57735,0.57735,-0.57735)
  Focus = 100
  HardHidden = false
  IsoCount = 0
  IsoHidden = false
  IsoVisible = false
  LockPosition = false
  Perspective = false
  Rotation = 0
  RotationVector = (1,0,0)
  ScaleType = 2
  ScrubCount = 1
  SeamHidden = false
  SeamVisible = false
  SmoothHidden = false
  SmoothVisible = true
  Source = -> [Assembly]
  Type = 0
  X = 148.5
  XDirection = (0,-0.707106,-0.707106)
  Y = 105
FEATURE [TechDraw::DrawPage] Page001
  KeepUpdated = true
  NextBalloonIndex = 1
  ProjectionType = 0
  Template = -> Template001
  Views = -> [View002]
note: 2 file-system paths scrubbed to <path> (originals preserved in the JSON sidecar)
---- part Assy_Stack_Module.FCStd = doc fcstd_b85c8f13e317 ----
FCSTD DOCUMENT  (FreeCAD 1.0R39319 (Git))
Label: Assy_Stack_Module
License: All rights reserved
LicenseURL: https://en.wikipedia.org/wiki/All_rights_reserved
objects: App::Link×5, Part::FeaturePython×4, App::DocumentObjectGroup×3, PartDesign::CoordinateSystem×1, App::FeaturePython×1, App::Part×1
note: 5 computed .brp shape members not serialized (recipe doc carries the construction recipe); baked Part::Feature solids carry a one-line shape summary decoded from their .brp
EXTERNAL_REF file=../../Part/Print/Stack_Module.FCStd obj=screen_ref
EXTERNAL_REF file=../../Part/Print/Stack_Module.FCStd obj=Part
EXTERNAL_REF file=../../Part/Print/Spacer.FCStd obj=LCS_1
EXTERNAL_REF file=../../Part/Print/Stack_Module.FCStd obj=spacer_att_1
EXTERNAL_REF file=../../Part/Print/Spacer.FCStd obj=Part
EXTERNAL_REF file=../../Part/Print/Stack_Module.FCStd obj=spacer_att_2
EXTERNAL_REF file=../../Part/Print/Stack_Module.FCStd obj=spacer_att_3
EXTERNAL_REF file=../../Part/Print/Stack_Module.FCStd obj=spacer_att_4

FEATURE [App::DocumentObjectGroup] Parts
FEATURE [PartDesign::CoordinateSystem] LCS_Origin
  AttacherType = Attacher::AttachEngine3D
  AttachmentSupport = -> [X_Axis]
  MapMode = 2
FEATURE [App::DocumentObjectGroup] Constraints
FEATURE [App::FeaturePython] Variables  # WARN: FeaturePython — macro-defined, semantics opaque (R4)
  Type = App::PropertyContainer
FEATURE [App::DocumentObjectGroup] Configurations
FEATURE [App::Link] Stack_Module
  AttachedBy = #screen_ref
  AttachedTo = Parent Assembly#LCS_Origin
  LinkPlacement = pos=(19.9856,50,3) rot=(0.57735,0.57735,0.57735;2.0944rad)
  LinkedObject = -> <external ../../Part/Print/Stack_Module.FCStd>#Part
  Placement = pos=(19.9856,50,3) rot=(0.57735,0.57735,0.57735;2.0944rad)
  SolverId = Asm4EE
  expr: Placement = LCS_Origin.Placement * AttachmentOffset * Stack_Module#screen_ref.Placement ^ -1
FEATURE [App::Link] Spacer
  AttachedBy = #LCS_1
  AttachedTo = Stack_Module#spacer_att_1
  LinkPlacement = pos=(-33.5144,116.5,-79.5) rot=(0.707107,0.707107,0;3.14159rad)
  LinkedObject = -> <external ../../Part/Print/Spacer.FCStd>#Part
  Placement = pos=(-33.5144,116.5,-79.5) rot=(0.707107,0.707107,0;3.14159rad)
  SolverId = Asm4EE
  expr: Placement = Stack_Module.Placement * Stack_Module#spacer_att_1.Placement * AttachmentOffset * Spacer#LCS_1.Placement ^ -1
FEATURE [App::Link] Spacer001
  AttachedBy = #LCS_1
  AttachedTo = Stack_Module#spacer_att_2
  LinkPlacement = pos=(82.4856,113.5,-79.5) rot=(0.707107,0.707107,0;3.14159rad)
  LinkedObject = -> <external ../../Part/Print/Spacer.FCStd>#Part
  Placement = pos=(82.4856,113.5,-79.5) rot=(0.707107,0.707107,0;3.14159rad)
  SolverId = Asm4EE
  expr: Placement = Stack_Module.Placement * Stack_Module#spacer_att_2.Placement * AttachmentOffset * Spacer#LCS_1.Placement ^ -1
FEATURE [App::Link] Spacer002
  AttachedBy = #LCS_1
  AttachedTo = Stack_Module#spacer_att_3
  AttachmentOffset = pos=(0,0,0) rot=(0,1,0;3.14159rad)
  LinkPlacement = pos=(-33.5144,-16.5,-79.5) rot=(0.707107,-0.707107,0;3.14159rad)
  LinkedObject = -> <external ../../Part/Print/Spacer.FCStd>#Part
  Placement = pos=(-33.5144,-16.5,-79.5) rot=(0.707107,-0.707107,0;3.14159rad)
  SolverId = Asm4EE
  expr: Placement = Stack_Module.Placement * Stack_Module#spacer_att_3.Placement * AttachmentOffset * Spacer#LCS_1.Placement ^ -1
FEATURE [App::Link] Spacer003
  AttachedBy = #LCS_1
  AttachedTo = Stack_Module#spacer_att_4
  AttachmentOffset = pos=(0,0,0) rot=(0,1,0;3.14159rad)
  LinkPlacement = pos=(82.4856,-13.5,-79.5) rot=(0.707107,-0.707107,0;3.14159rad)
  LinkedObject = -> <external ../../Part/Print/Spacer.FCStd>#Part
  Placement = pos=(82.4856,-13.5,-79.5) rot=(0.707107,-0.707107,0;3.14159rad)
  SolverId = Asm4EE
  expr: Placement = Stack_Module.Placement * Stack_Module#spacer_att_4.Placement * AttachmentOffset * Spacer#LCS_1.Placement ^ -1
FEATURE [Part::FeaturePython] Screw  label="M5x10-Screw"  # WARN: FeaturePython — macro-defined, semantics opaque (R4)
  BaseObject = -> Stack_Module [Body.Mirrored.Edge531]
  Diameter = 3
  Invert = true
  LeftHanded = false
  Length = 1
  LengthCustom = 10
  MatchOuter = false
  OffsetAngle = 0
  Placement = pos=(-31.0144,2.23e-14,-3) rot=(0.830469,-0.557065,0;3.14159rad)
  Thread = false
  Type = 86
FEATURE [Part::FeaturePython] Screw001  label="M5x10-Screw007"  # WARN: FeaturePython — macro-defined, semantics opaque (R4)
  BaseObject = -> Stack_Module [Body.Mirrored.Edge537]
  Diameter = 3
  Invert = true
  LeftHanded = false
  Length = 1
  LengthCustom = 10
  MatchOuter = false
  OffsetAngle = 0
  Placement = pos=(35.9856,8.1e-15,-3) rot=(0.830469,-0.557065,0;3.14159rad)
  Thread = false
  Type = 86
FEATURE [Part::FeaturePython] Screw002  label="M5x10-Screw008"  # WARN: FeaturePython — macro-defined, semantics opaque (R4)
  BaseObject = -> Stack_Module [Body.Mirrored.Edge265]
  Diameter = 3
  Invert = false
  LeftHanded = false
  Length = 1
  LengthCustom = 10
  MatchOuter = false
  OffsetAngle = 0
  Placement = pos=(35.9856,100,-3) rot=(-1,0,0;3.14159rad)
  Thread = false
  Type = 86
FEATURE [Part::FeaturePython] Screw003  label="M5x10-Screw009"  # WARN: FeaturePython — macro-defined, semantics opaque (R4)
  BaseObject = -> Stack_Module [Body.Mirrored.Edge258]
  Diameter = 3
  Invert = false
  LeftHanded = false
  Length = 1
  LengthCustom = 10
  MatchOuter = false
  OffsetAngle = 0
  Placement = pos=(-31.0144,100,-3) rot=(-1,0,0;3.14159rad)
  Thread = false
  Type = 86
FEATURE [App::Part] Assembly  label="Assy_Stack_Module"
  AssemblyType = Part::Link
  Group = -> [LCS_Origin,Constraints,Variables,Configurations,Stack_Module,Spacer,Spacer001,Spacer002,Spacer003,Screw,Screw001,Screw002,Screw003]
  Origin = -> Origin
  Type = Assembly
